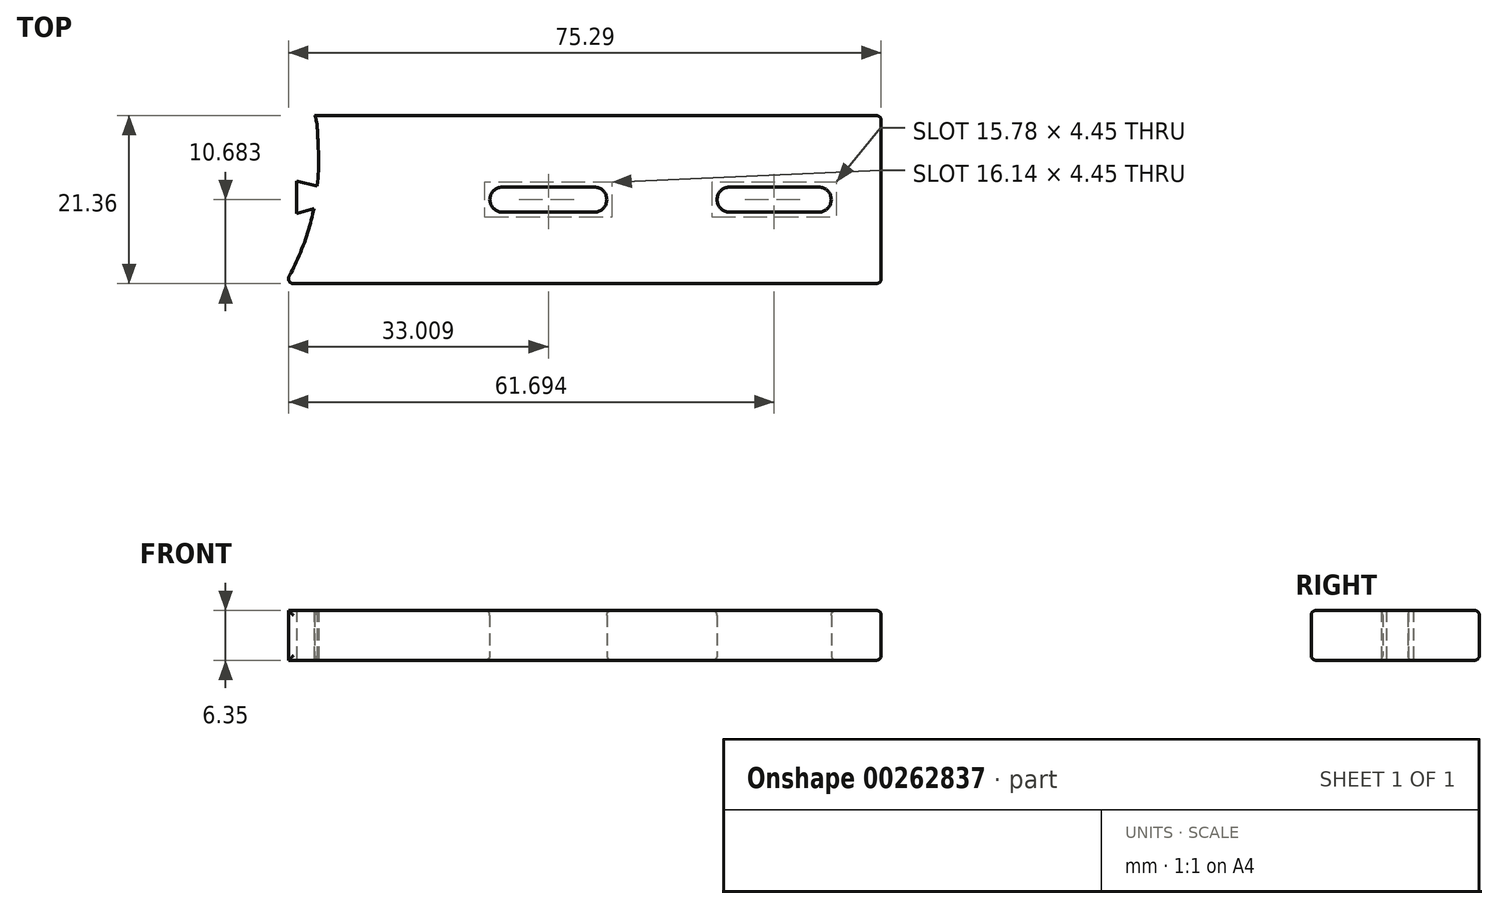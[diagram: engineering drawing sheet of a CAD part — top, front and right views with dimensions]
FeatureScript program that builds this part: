
annotation { "Feature Type Name" : "Feature", "Feature Type Description" : "" }
export const myFeature = defineFeature(function(context is Context, id is Id, definition is map)
    precondition{}
    {
        {
            var Q0;
            Q0=qCreatedBy(makeId("Top.planeOp"),FACE);
            var sketch = newSketch(context, id + "F0", { "sketchPlane" : qUnion([Q0])});
            skLineSegment(sketch, "E0.bottom", {"start": v(-38.99, -10.7) * mm, "end": v(37.21, -10.7) * mm});
            skLineSegment(sketch, "E0.right", {"start": v(37.21, -10.7) * mm, "end": v(37.21, 10.66) * mm});
            skLineSegment(sketch, "E1", {"start": v(37.21, 10.66) * mm, "end": v(-34.73, 10.66) * mm});
            skFitSpline(sketch, "E2", {"points": [v(-38.99, -10.7) * mm, v(-37.86, -9.52) * mm, v(-36.06, -5.46) * mm, v(-34.86, -1.18) * mm], "startDerivative": vector(8.3, 5.04) * mm, "endDerivative": vector(2.06, 9.8) * mm});
            skPoint(sketch, "E3.1.internal.snap0", {"position": v(-34.6, 9.73) * mm});
            skFitSpline(sketch, "E3", {"points": [v(-34.73, 10.66) * mm, v(-34.49, 9.73) * mm, v(-34.32, 7.04) * mm, v(-34.42, 1.67) * mm], "startDerivative": vector(1.51, -3.86) * mm, "endDerivative": vector(-1.7, -14.48) * mm});
            skLineSegment(sketch, "E4", {"start": v(-34.42, 1.67) * mm, "end": v(-37.05, 2.3) * mm});
            skLineSegment(sketch, "E5", {"start": v(-37.05, 2.3) * mm, "end": v(-37.05, -1.8) * mm});
            skLineSegment(sketch, "E6", {"start": v(-37.05, -1.8) * mm, "end": v(-34.73, -1.14) * mm});
            skPoint(sketch, "E7", {"position": v(-38.35, -10.18) * mm});
            skPoint(sketch, "E8.center.orphan", {"position": v(12.01, -0.02) * mm});
            skPoint(sketch, "E9.orphan", {"position": v(17.95, -10.7) * mm});
            skPoint(sketch, "E10.end.orphan", {"position": v(17.95, 10.66) * mm});
            skPoint(sketch, "E11.start.orphan", {"position": v(37.21, -0.02) * mm});
            skLineSegment(sketch, "E12", {"start": v(29.28, -10.7) * mm, "end": v(29.28, 10.66) * mm, "construction": true});
            skLineSegment(sketch, "E13", {"start": v(17.95, -10.7) * mm, "end": v(17.95, 10.66) * mm, "construction": true});
            skLineSegment(sketch, "E14", {"start": v(0.77, -10.7) * mm, "end": v(0.77, 10.66) * mm, "construction": true});
            skLineSegment(sketch, "E15", {"start": v(-10.92, -10.7) * mm, "end": v(-10.92, 10.66) * mm, "construction": true});
            skLineSegment(sketch, "E16", {"start": v(-10.92, -0.02) * mm, "end": v(0.77, -0.02) * mm, "construction": true});
            skLineSegment(sketch, "E17", {"start": v(17.95, -0.02) * mm, "end": v(29.28, -0.02) * mm, "construction": true});
            skArc(sketch, "E18.0.startCap", {"start": v(17.95, -1.6) * mm, "mid": v(16.36, -0.02) * mm, "end": v(17.95, 1.57) * mm});
            skArc(sketch, "E18.0.endCap", {"start": v(29.28, 1.57) * mm, "mid": v(30.87, -0.02) * mm, "end": v(29.28, -1.6) * mm});
            skLineSegment(sketch, "E18.0.left", {"start": v(17.95, 1.57) * mm, "end": v(29.28, 1.57) * mm});
            skLineSegment(sketch, "E18.0.right", {"start": v(17.95, -1.6) * mm, "end": v(29.28, -1.6) * mm});
            skArc(sketch, "E19.0.startCap", {"start": v(-10.92, -1.6) * mm, "mid": v(-12.5, -0.02) * mm, "end": v(-10.92, 1.57) * mm});
            skArc(sketch, "E19.0.endCap", {"start": v(0.77, 1.57) * mm, "mid": v(2.36, -0.02) * mm, "end": v(0.77, -1.6) * mm});
            skLineSegment(sketch, "E19.0.left", {"start": v(-10.92, 1.57) * mm, "end": v(0.77, 1.57) * mm});
            skLineSegment(sketch, "E19.0.right", {"start": v(-10.92, -1.6) * mm, "end": v(0.77, -1.6) * mm});
            skSolve(sketch);
        }
        {
            var Q0;
            Q0=makeQuery(id+"F0.imprint","IMPRINT",FACE,{"disambiguationData":[TD([[makeQuery(id+"F0.imprint","IMPRINT",EDGE,{"derivedFrom":sQuery(id+"F0.wireOp",EDGE,"E0.bottom")}),1.0]])]});
            extrude(context, id + "F1", {"entities" : qUnion([Q0]), "depth" : 6.35 * mm});
        }
        {
            var Q0;
            Q0=makeQuery(id+"F1.opExtrude","SWEPT_FACE",FACE,{"disambiguationData":[OSD([sQuery(id+"F0.wireOp",EDGE,"E0.bottom")])]});
            var Q1;
            Q1=makeQuery(id+"F1.opExtrude","CAP_EDGE",EDGE,{"disambiguationData":[OSD([sQuery(id+"F0.wireOp",EDGE,"E0.right")])],"isStart":true});
            var Q2;
            Q2=makeQuery(id+"F1.opExtrude","SWEPT_FACE",FACE,{"disambiguationData":[OSD([sQuery(id+"F0.wireOp",EDGE,"E0.right")])]});
            var Q3;
            Q3=makeQuery(id+"F1.opExtrude","CAP_EDGE",EDGE,{"disambiguationData":[OSD([sQuery(id+"F0.wireOp",EDGE,"E1")])],"isStart":false});
            var Q4;
            Q4=makeQuery(id+"F1.opExtrude","CAP_EDGE",EDGE,{"disambiguationData":[OSD([sQuery(id+"F0.wireOp",EDGE,"E1")])],"isStart":true});
            var Q5;
            Q5=makeQuery(id+"F1.opExtrude","SWEPT_FACE",FACE,{"disambiguationData":[OSD([sQuery(id+"F0.wireOp",EDGE,"E19.0.left")])]});
            var Q6;
            Q6=makeQuery(id+"F1.opExtrude","SWEPT_FACE",FACE,{"disambiguationData":[OSD([sQuery(id+"F0.wireOp",EDGE,"E18.0.left")])]});
            fillet(context, id + "F2", {"entities" : qUnion([Q0, Q1, Q2, Q3, Q4, Q5, Q6]), "radius" : 0.64 * mm, "tangentPropagation" : true, "allowEdgeOverflow" : false});
        }
    });
